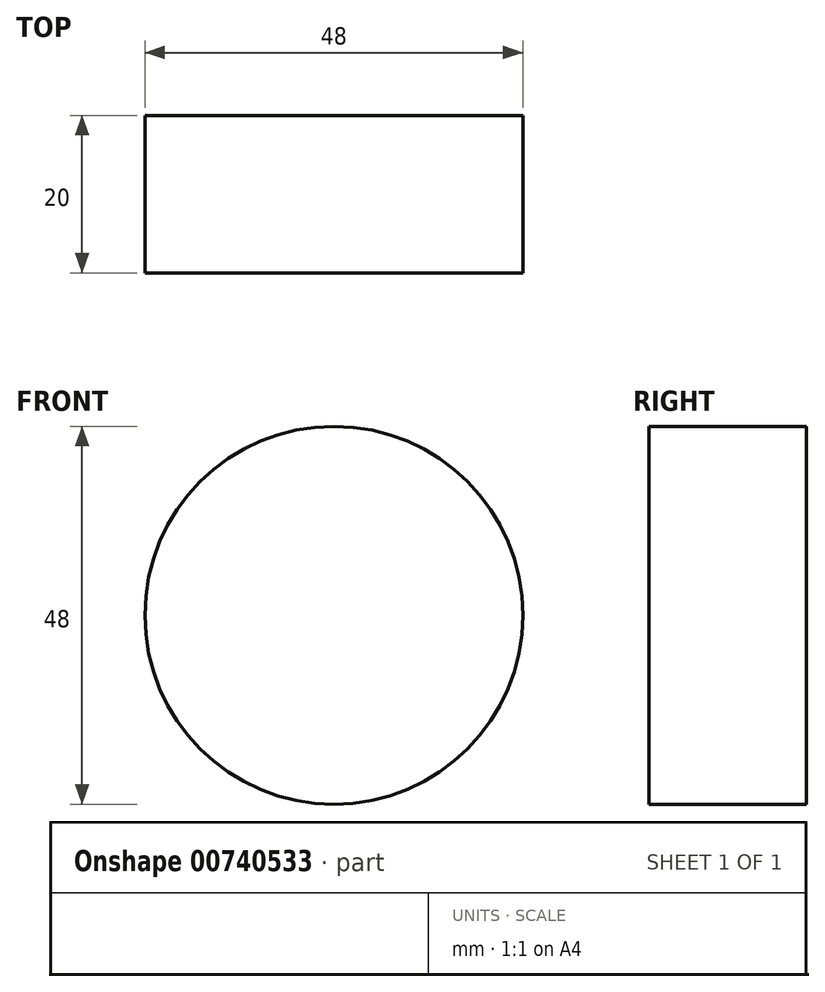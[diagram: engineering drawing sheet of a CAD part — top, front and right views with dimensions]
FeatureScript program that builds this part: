
annotation { "Feature Type Name" : "Feature", "Feature Type Description" : "" }
export const myFeature = defineFeature(function(context is Context, id is Id, definition is map)
    precondition{}
    {
        {
            var Q0;
            Q0=qCreatedBy(makeId("Front.planeOp"),FACE);
            var sketch = newSketch(context, id + "F0", { "sketchPlane" : qUnion([Q0])});
            skCircle(sketch, "E0", {"center": v(0, 0) * mm, "radius": 50 * mm});
            skCircle(sketch, "E1", {"center": v(138, 0) * mm, "radius": 24 * mm});
            skCircle(sketch, "E2", {"center": v(0, 0) * mm, "radius": 39 * mm});
            skLineSegment(sketch, "E3", {"start": v(0, 0) * mm, "end": v(27.58, 27.58) * mm});
            skCircle(sketch, "E4", {"center": v(27.58, 27.58) * mm, "radius": 4.25 * mm});
            skLineSegment(sketch, "E5", {"start": v(11.77, 48.6) * mm, "end": v(141.32, 23.8) * mm});
            skLineSegment(sketch, "E6", {"start": v(0, -50) * mm, "end": v(139.31, -23.96) * mm});
            skSolve(sketch);
        }
        {
            var Q0;
            Q0=makeQuery(id+"F0.imprint","IMPRINT",FACE,{"disambiguationData":[TD([[makeQuery(id+"F0.imprint","IMPRINT",EDGE,{"derivedFrom":sQuery(id+"F0.wireOp",EDGE,"E1")}),1.0]])]});
            extrude(context, id + "F1", {"entities" : qUnion([Q0]), "depth" : 20 * mm, "offsetDistance" : 25 * mm});
        }
    });
